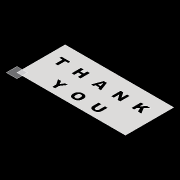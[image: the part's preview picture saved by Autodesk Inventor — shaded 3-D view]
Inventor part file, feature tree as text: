
AUTODESK INVENTOR PART (.ipt)
format: ipt  version: 2018 (Build 220112000, 112)  size: 123,392 bytes
history: native  units: mm
features: plane x1, sketch x1, other x1, surface_op x1
ambient origin geometry x8: Origin, YZ Plane, XZ Plane, XY Plane, X Axis, Y Axis, Z Axis, Center Point
bodies: Body1 (feature_tree)
feature tree (4):
  plane  "Work Plane5"
  sketch  "Sketch6"  dims[d17=225.0mm d18=100.0mm]
  other  "Srf3"
  surface_op  "Boundary Patch3"
